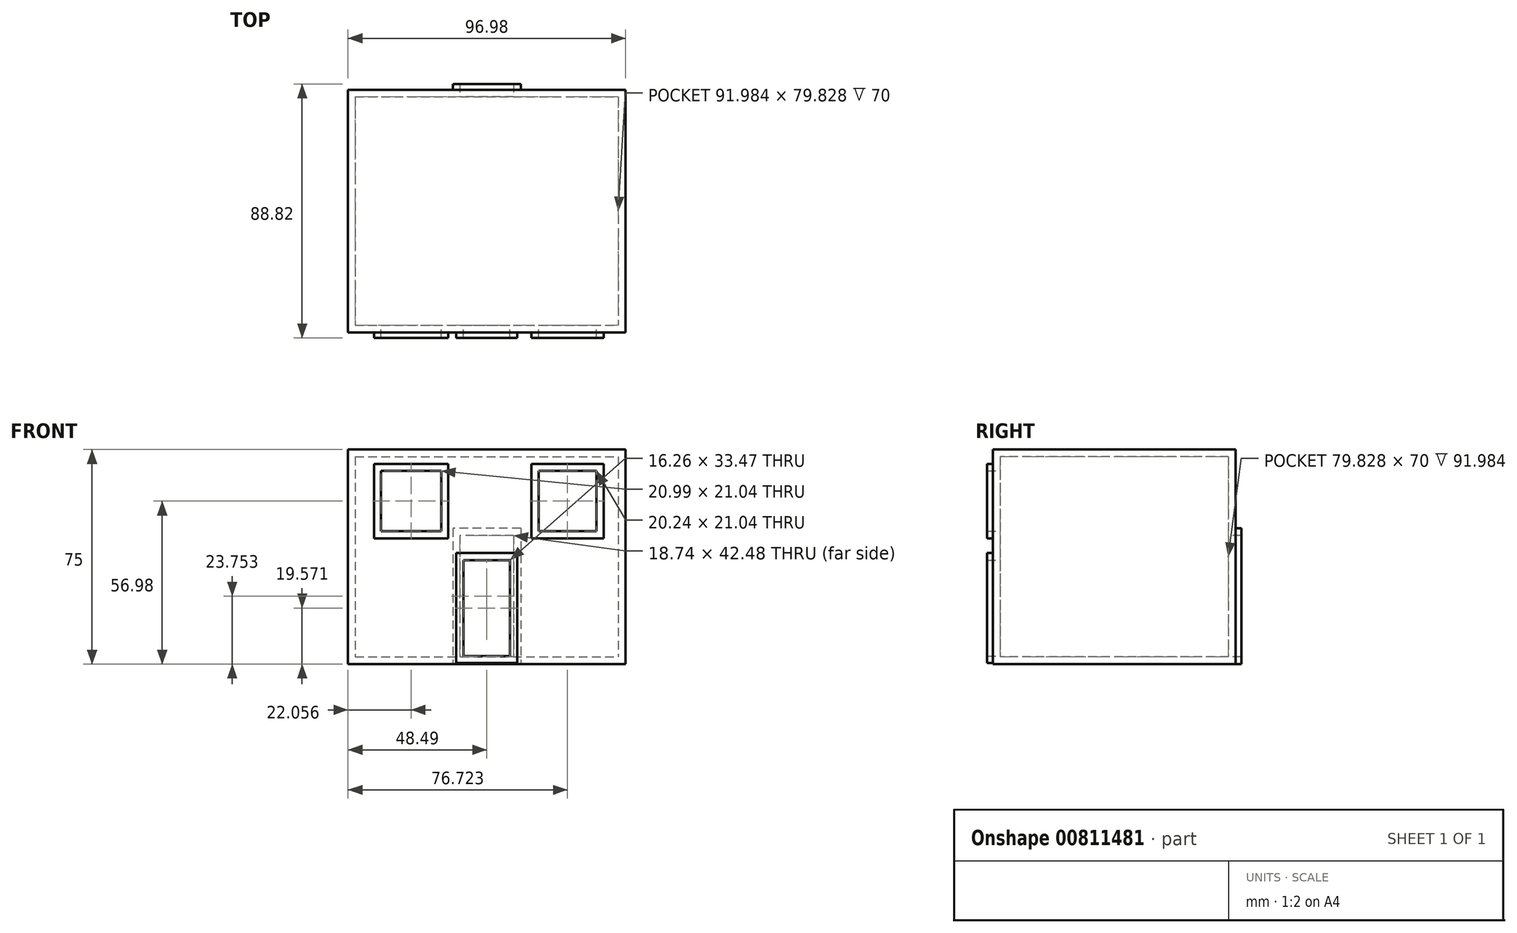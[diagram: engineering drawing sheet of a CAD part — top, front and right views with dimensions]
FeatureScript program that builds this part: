
annotation { "Feature Type Name" : "Feature", "Feature Type Description" : "" }
export const myFeature = defineFeature(function(context is Context, id is Id, definition is map)
    precondition{}
    {
        {
            var Q0;
            Q0=qCreatedBy(makeId("Top.planeOp"),FACE);
            var sketch = newSketch(context, id + "F0", { "sketchPlane" : qUnion([Q0])});
            skLineSegment(sketch, "E0.bottom", {"start": v(-48.5, 42.41) * mm, "end": v(48.5, 42.41) * mm});
            skLineSegment(sketch, "E0.top", {"start": v(-48.5, -42.41) * mm, "end": v(48.5, -42.41) * mm});
            skLineSegment(sketch, "E0.left", {"start": v(-48.5, 42.41) * mm, "end": v(-48.5, -42.41) * mm});
            skLineSegment(sketch, "E0.right", {"start": v(48.5, 42.41) * mm, "end": v(48.5, -42.41) * mm});
            skPoint(sketch, "E0.middle", {"position": v(0, 0) * mm});
            skSolve(sketch);
        }
        {
            var Q0;
            Q0 = qSketchRegion(id + "F0", true);
            extrude(context, id + "F1", {"entities" : qUnion([Q0]), "depth" : 75 * mm, "offsetDistance" : 25 * mm});
        }
        {
            var Q0;
            Q0=makeQuery(id+"F1.opExtrude","SWEPT_FACE",FACE,{"disambiguationData":[OSD([sQuery(id+"F0.wireOp",EDGE,"E0.top")])]});
            var sketch = newSketch(context, id + "F2", { "sketchPlane" : qUnion([Q0])});
            skLineSegment(sketch, "E1.bottom", {"start": v(-10.63, 38.8) * mm, "end": v(10.63, 38.8) * mm});
            skLineSegment(sketch, "E1.top", {"start": v(-10.63, 0.33) * mm, "end": v(10.63, 0.33) * mm});
            skLineSegment(sketch, "E1.left", {"start": v(-10.63, 38.8) * mm, "end": v(-10.63, 0.33) * mm});
            skLineSegment(sketch, "E1.right", {"start": v(10.63, 38.8) * mm, "end": v(10.63, 0.33) * mm});
            skPoint(sketch, "E1.middle", {"position": v(0, 19.57) * mm});
            skSolve(sketch);
        }
        {
            var Q0;
            Q0 = qSketchRegion(id + "F2", true);
            extrude(context, id + "F3", {"entities" : qUnion([Q0]), "operationType" : NewBodyOperationType.ADD, "depth" : 2 * mm, "offsetDistance" : 25 * mm});
        }
        {
            var Q0;
            Q0=makeQuery(id+"F1.opExtrude","SWEPT_FACE",FACE,{"disambiguationData":[OSD([sQuery(id+"F0.wireOp",EDGE,"E0.top")])]});
            var sketch = newSketch(context, id + "F4", { "sketchPlane" : qUnion([Q0])});
            skLineSegment(sketch, "E2.bottom", {"start": v(-39.43, 70) * mm, "end": v(-13.44, 70) * mm});
            skLineSegment(sketch, "E2.top", {"start": v(-39.43, 43.96) * mm, "end": v(-13.44, 43.96) * mm});
            skLineSegment(sketch, "E2.left", {"start": v(-39.43, 70) * mm, "end": v(-39.43, 43.96) * mm});
            skLineSegment(sketch, "E2.right", {"start": v(-13.44, 70) * mm, "end": v(-13.44, 43.96) * mm});
            skPoint(sketch, "E2.middle", {"position": v(-26.43, 56.98) * mm});
            skLineSegment(sketch, "E3.bottom", {"start": v(15.61, 70) * mm, "end": v(40.85, 70) * mm});
            skLineSegment(sketch, "E3.top", {"start": v(15.61, 43.96) * mm, "end": v(40.85, 43.96) * mm});
            skLineSegment(sketch, "E3.left", {"start": v(15.61, 70) * mm, "end": v(15.61, 43.96) * mm});
            skLineSegment(sketch, "E3.right", {"start": v(40.85, 70) * mm, "end": v(40.85, 43.96) * mm});
            skPoint(sketch, "E3.middle", {"position": v(28.23, 56.98) * mm});
            skSolve(sketch);
        }
        {
            var Q0;
            Q0 = qSketchRegion(id + "F4", true);
            extrude(context, id + "F5", {"entities" : qUnion([Q0]), "operationType" : NewBodyOperationType.ADD, "depth" : 2 * mm, "offsetDistance" : 25 * mm});
        }
        {
            var Q0;
            Q0=makeQuery(id+"F1.opExtrude","SWEPT_FACE",FACE,{"disambiguationData":[OSD([sQuery(id+"F0.wireOp",EDGE,"E0.bottom")])]});
            var sketch = newSketch(context, id + "F6", { "sketchPlane" : qUnion([Q0])});
            skPoint(sketch, "E4.middle", {"position": v(0, 29.61) * mm});
            skLineSegment(sketch, "E5.bottom", {"start": v(-11.87, 47.5) * mm, "end": v(11.87, 47.5) * mm});
            skLineSegment(sketch, "E5.top", {"start": v(-11.87, 0.01) * mm, "end": v(11.87, 0.01) * mm});
            skLineSegment(sketch, "E5.left", {"start": v(-11.87, 47.5) * mm, "end": v(-11.87, 0.01) * mm});
            skLineSegment(sketch, "E5.right", {"start": v(11.87, 47.5) * mm, "end": v(11.87, 0.01) * mm});
            skPoint(sketch, "E5.middle", {"position": v(0, 23.75) * mm});
            skSolve(sketch);
        }
        {
            var Q0;
            Q0 = qSketchRegion(id + "F6", true);
            extrude(context, id + "F7", {"entities" : qUnion([Q0]), "operationType" : NewBodyOperationType.ADD, "depth" : 2 * mm, "offsetDistance" : 25 * mm});
        }
        {
            var Q0;
            Q0=makeQuery(id+"F7.opExtrude","CAP_FACE",FACE,{"disambiguationData":[OSD([sQuery(id+"F6.wireOp",EDGE,"E5.bottom"),sQuery(id+"F6.wireOp",EDGE,"E5.top"),sQuery(id+"F6.wireOp",EDGE,"E5.left"),sQuery(id+"F6.wireOp",EDGE,"E5.right")])],"isStart":false});
            var Q1;
            Q1=makeQuery(id+"F5.opExtrude","CAP_FACE",FACE,{"disambiguationData":[OSD([sQuery(id+"F4.wireOp",EDGE,"E2.bottom"),sQuery(id+"F4.wireOp",EDGE,"E2.top"),sQuery(id+"F4.wireOp",EDGE,"E2.left"),sQuery(id+"F4.wireOp",EDGE,"E2.right")])],"isStart":false});
            var Q2;
            Q2=makeQuery(id+"F5.opExtrude","CAP_FACE",FACE,{"disambiguationData":[OSD([sQuery(id+"F4.wireOp",EDGE,"E3.bottom"),sQuery(id+"F4.wireOp",EDGE,"E3.top"),sQuery(id+"F4.wireOp",EDGE,"E3.left"),sQuery(id+"F4.wireOp",EDGE,"E3.right")])],"isStart":false});
            var Q3;
            Q3=makeQuery(id+"F3.opExtrude","CAP_FACE",FACE,{"disambiguationData":[OSD([sQuery(id+"F2.wireOp",EDGE,"E1.bottom"),sQuery(id+"F2.wireOp",EDGE,"E1.top"),sQuery(id+"F2.wireOp",EDGE,"E1.left"),sQuery(id+"F2.wireOp",EDGE,"E1.right")])],"isStart":false});
            shell(context, id + "F8", {"entities" : qUnion([Q0, Q1, Q2, Q3]), "thickness" : 2.5 * mm});
        }
    });
